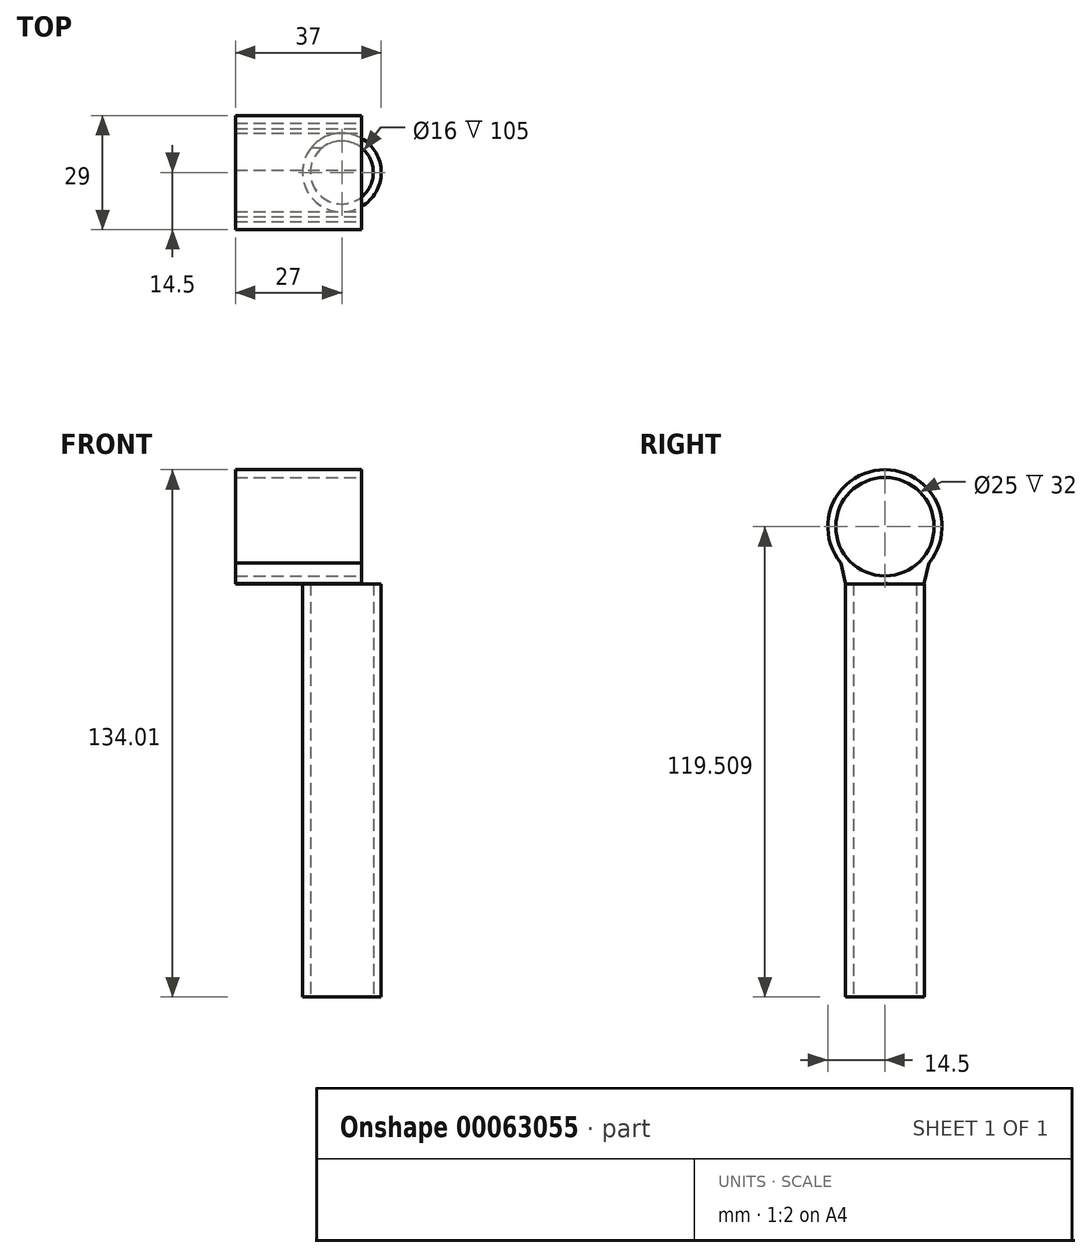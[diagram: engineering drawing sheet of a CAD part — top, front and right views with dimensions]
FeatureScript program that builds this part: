
annotation { "Feature Type Name" : "Feature", "Feature Type Description" : "" }
export const myFeature = defineFeature(function(context is Context, id is Id, definition is map)
    precondition{}
    {
        {
            var Q0;
            Q0=qCreatedBy(makeId("Top.planeOp"),FACE);
            var sketch = newSketch(context, id + "F0", { "sketchPlane" : qUnion([Q0])});
            skCircle(sketch, "E0", {"center": v(0, 0) * mm, "radius": 8 * mm});
            skCircle(sketch, "E1", {"center": v(0, 0) * mm, "radius": 10 * mm});
            skSolve(sketch);
        }
        {
            var Q0;
            Q0 = qSketchRegion(id + "F0", true);
            var Q1;
            Q1=makeQuery(id+"F0.imprint","IMPRINT",FACE,{"disambiguationData":[TD([[makeQuery(id+"F0.imprint","IMPRINT",EDGE,{"derivedFrom":sQuery(id+"F0.wireOp",EDGE,"E0")}),-1.0]])]});
            extrude(context, id + "F1", {"entities" : qUnion([Q0, Q1]), "depth" : 105 * mm});
        }
        {
            var Q0;
            Q0=qCreatedBy(makeId("Right.planeOp"),FACE);
            var Q1;
            Q1=makeQuery(id+"F1.opExtrude","CAP_EDGE",EDGE,{"disambiguationData":[OSD([sQuery(id+"F0.wireOp",EDGE,"E1")])],"isStart":false});
            cPlane(context, id + "F2", {"entities" : qUnion([Q0, Q1]), "cplaneType" : CPlaneType.LINE_ANGLE, "offset" : 0 * mm, "angle" : 0 * degree, "width" : 152.4 * mm, "height" : 152.4 * mm});
        }
        {
            var Q0;
            Q0=qCreatedBy(id+"F2.planeOp",FACE);
            var sketch = newSketch(context, id + "F3", { "sketchPlane" : qUnion([Q0])});
            skCircle(sketch, "E2", {"center": v(0, 119.5) * mm, "radius": 14.5 * mm});
            skLineSegment(sketch, "E3", {"start": v(11.17, 110.27) * mm, "end": v(9.97, 105.05) * mm});
            skLineSegment(sketch, "E4", {"start": v(9.97, 105.05) * mm, "end": v(0, 105) * mm});
            skLineSegment(sketch, "E5.MirrorCS", {"start": v(-11.16, 110.25) * mm, "end": v(-9.95, 104.99) * mm});
            skLineSegment(sketch, "E6.MirrorCS", {"start": v(-9.95, 104.99) * mm, "end": v(0.02, 105.02) * mm});
            skCircle(sketch, "E7", {"center": v(0, 119.5) * mm, "radius": 12.5 * mm});
            skSolve(sketch);
        }
        {
            var Q0;
            Q0=makeQuery(id+"F3.imprint","IMPRINT",FACE,{"disambiguationData":[TD([[makeQuery(id+"F3.imprint","IMPRINT",EDGE,{"derivedFrom":sQuery(id+"F3.wireOp",EDGE,"E7")}),-1.0]])]});
            var Q1;
            {var subQ0=sQuery(id+"F3.wireOp",EDGE,"E5.MirrorCS");Q1=makeQuery(id+"F3.imprint","IMPRINT",FACE,{"disambiguationData":[TD([[makeQuery(id+"F3.imprint","IMPRINT",EDGE,{"derivedFrom":subQ0}),1.0]])]});}
            var Q2;
            {var subQ0=sQuery(id+"F3.wireOp",EDGE,"E3");Q2=makeQuery(id+"F3.imprint","IMPRINT",FACE,{"disambiguationData":[TD([[makeQuery(id+"F3.imprint","IMPRINT",EDGE,{"derivedFrom":subQ0}),-1.0]])]});}
            extrude(context, id + "F4", {"entities" : qUnion([Q0, Q1, Q2]), "operationType" : NewBodyOperationType.ADD, "depth" : 27 * mm, "hasSecondDirection" : true, "secondDirectionOppositeDirection" : true, "secondDirectionDepth" : 5 * mm});
        }
    });
